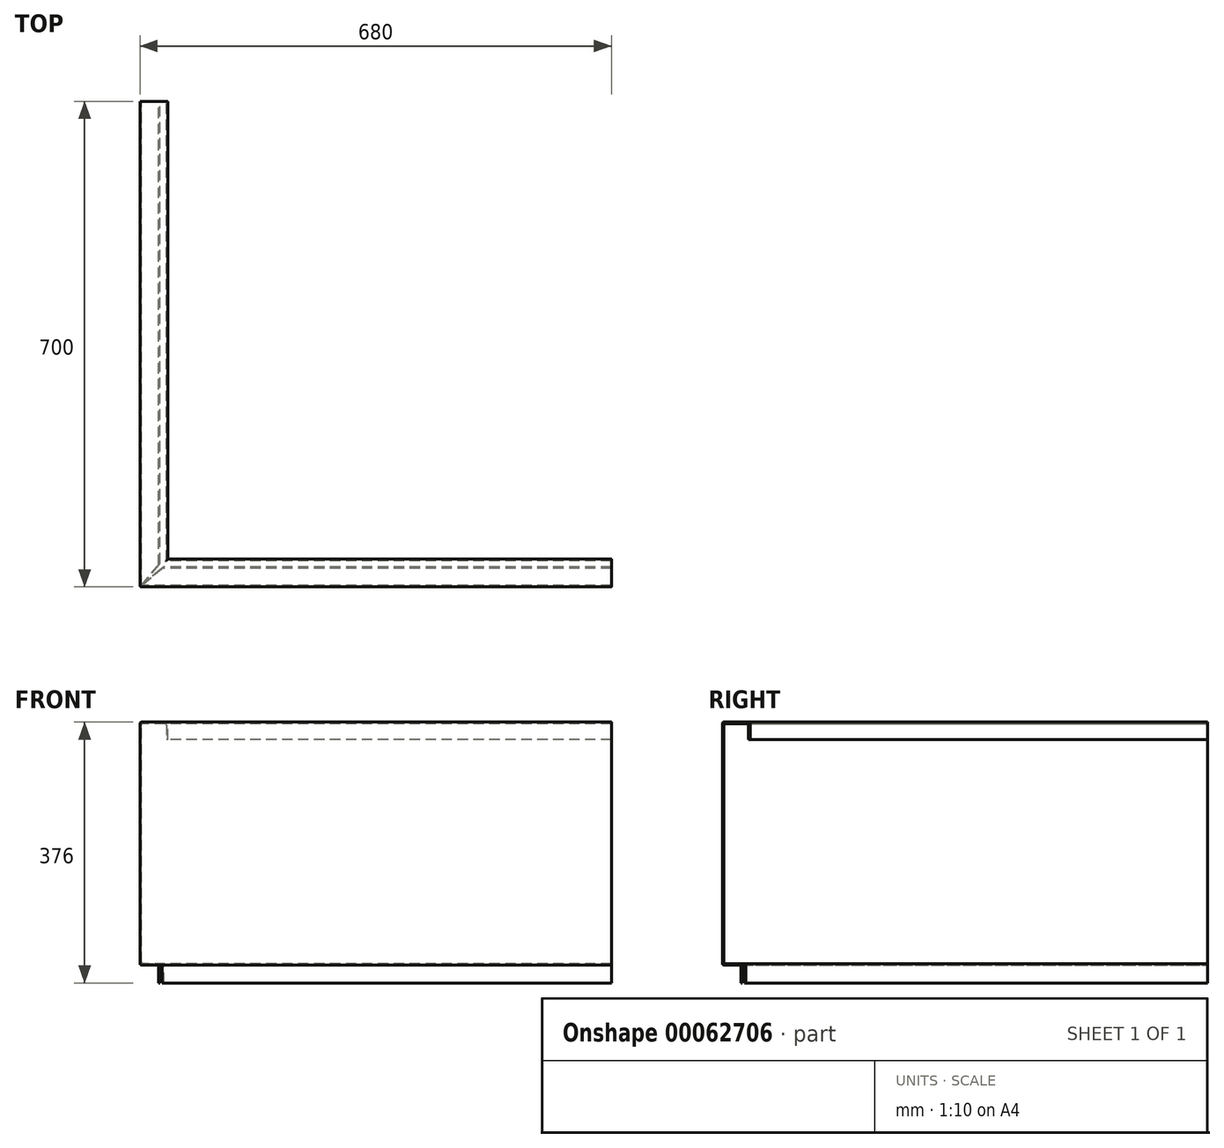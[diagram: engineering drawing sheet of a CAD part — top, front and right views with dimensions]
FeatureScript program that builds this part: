
annotation { "Feature Type Name" : "Feature", "Feature Type Description" : "" }
export const myFeature = defineFeature(function(context is Context, id is Id, definition is map)
    precondition{}
    {
        {
            var Q0;
            Q0=qCreatedBy(makeId("Right.planeOp"),FACE);
            var sketch = newSketch(context, id + "F0", { "sketchPlane" : qUnion([Q0])});
            skLineSegment(sketch, "E0.0", {"start": v(0, -350) * mm, "end": v(27, -350) * mm});
            skLineSegment(sketch, "E0.1", {"start": v(0, 0) * mm, "end": v(0, -350) * mm});
            skLineSegment(sketch, "E1", {"start": v(2, -348) * mm, "end": v(29, -348) * mm});
            skLineSegment(sketch, "E2", {"start": v(2, -2) * mm, "end": v(2, -348) * mm});
            skLineSegment(sketch, "E3", {"start": v(38, -2) * mm, "end": v(2, -2) * mm});
            skLineSegment(sketch, "E4", {"start": v(38, -25) * mm, "end": v(38, -2) * mm});
            skLineSegment(sketch, "E5", {"start": v(27, -350) * mm, "end": v(27, -376) * mm});
            skLineSegment(sketch, "E6", {"start": v(29, -348) * mm, "end": v(29, -376) * mm});
            skLineSegment(sketch, "E0.2", {"start": v(40, 0) * mm, "end": v(0, 0) * mm});
            skLineSegment(sketch, "E0.3", {"start": v(40, -25) * mm, "end": v(40, 0) * mm});
            skLineSegment(sketch, "E7", {"start": v(40, -25) * mm, "end": v(38, -25) * mm});
            skLineSegment(sketch, "E8", {"start": v(29, -376) * mm, "end": v(27, -376) * mm});
            skSolve(sketch);
        }
        {
            var Q0;
            Q0=qCreatedBy(makeId("Top.planeOp"),FACE);
            var sketch = newSketch(context, id + "F1", { "sketchPlane" : qUnion([Q0])});
            skLineSegment(sketch, "E9", {"start": v(0, 0) * mm, "end": v(-680, 0) * mm});
            skLineSegment(sketch, "E10", {"start": v(-680, 0) * mm, "end": v(-680, 700) * mm});
            skSolve(sketch);
        }
        {
            var Q0;
            Q0=qSketchRegion(id+"F0",true);
            var Q1;
            Q1=qConstructionFilter(qBodyType(qCreatedBy(id+"F1",EDGE),BodyType.WIRE),ConstructionObject.NO);
            sweep(context, id + "F2", {"profiles" : qUnion([Q0]), "path" : qUnion([Q1])});
        }
        {
            var Q0;
            Q0=makeQuery(id+"F2.opSweep","SWEPT_FACE",FACE,{"disambiguationData":[OSD([sQuery(id+"F0.wireOp",EDGE,"E1"),sQuery(id+"F1.wireOp",EDGE,"E9")])]});
            var sketch = newSketch(context, id + "F3", { "sketchPlane" : qUnion([Q0])});
            skLineSegment(sketch, "E11", {"start": v(-678, 2) * mm, "end": v(-645.82, 29) * mm});
            skLineSegment(sketch, "E12", {"start": v(-645.82, 29) * mm, "end": v(-651, 29) * mm});
            skLineSegment(sketch, "E13", {"start": v(-651, 29) * mm, "end": v(-651, 34.18) * mm});
            skLineSegment(sketch, "E14", {"start": v(-651, 34.18) * mm, "end": v(-678, 2) * mm});
            skSolve(sketch);
        }
        {
            var Q0;
            Q0=qSketchRegion(id+"F3",true);
            extrude(context, id + "F4", {"entities" : qUnion([Q0]), "operationType" : NewBodyOperationType.REMOVE, "oppositeDirection" : true, "depth" : 30 * mm});
        }
        {
            var Q0;
            Q0=makeQuery(id+"F2.opSweep","SWEPT_EDGE",EDGE,{"disambiguationData":[OSD([sQuery(id+"F0.wireOp",EDGE,"E0.2"),sQuery(id+"F0.wireOp",EDGE,"E0.3"),sQuery(id+"F1.wireOp",EDGE,"E10")])]});
            var Q1;
            Q1=makeQuery(id+"F2.opSweep","SWEPT_EDGE",EDGE,{"disambiguationData":[OSD([sQuery(id+"F0.wireOp",EDGE,"E0.2"),sQuery(id+"F0.wireOp",EDGE,"E0.3"),sQuery(id+"F1.wireOp",EDGE,"E9")])]});
            var Q2;
            Q2=makeQuery(id+"F2.opSweep","SWEPT_EDGE",EDGE,{"disambiguationData":[OSD([sQuery(id+"F0.wireOp",EDGE,"E0.1"),sQuery(id+"F0.wireOp",EDGE,"E0.2"),sQuery(id+"F1.wireOp",EDGE,"E10")])]});
            var Q3;
            Q3=makeQuery(id+"F2.opSweep","SWEPT_EDGE",EDGE,{"disambiguationData":[OSD([sQuery(id+"F0.wireOp",EDGE,"E0.1"),sQuery(id+"F0.wireOp",EDGE,"E0.2"),sQuery(id+"F1.wireOp",EDGE,"E9")])]});
            var Q4;
            Q4=makeQuery(id+"F2.opSweep","SWEPT_EDGE",EDGE,{"disambiguationData":[OSD([sQuery(id+"F0.wireOp",EDGE,"E0.0"),sQuery(id+"F0.wireOp",EDGE,"E0.1"),sQuery(id+"F1.wireOp",EDGE,"E9")])]});
            var Q5;
            Q5=makeQuery(id+"F2.opSweep","SWEPT_EDGE",EDGE,{"disambiguationData":[OSD([sQuery(id+"F0.wireOp",EDGE,"E0.0"),sQuery(id+"F0.wireOp",EDGE,"E5"),sQuery(id+"F1.wireOp",EDGE,"E9")])]});
            var Q6;
            Q6=makeQuery(id+"F2.opSweep","SWEPT_EDGE",EDGE,{"disambiguationData":[OSD([sQuery(id+"F0.wireOp",EDGE,"E0.0"),sQuery(id+"F0.wireOp",EDGE,"E0.1"),sQuery(id+"F1.wireOp",EDGE,"E10")])]});
            var Q7;
            Q7=makeQuery(id+"F2.opSweep","SWEPT_EDGE",EDGE,{"disambiguationData":[OSD([sQuery(id+"F0.wireOp",EDGE,"E0.0"),sQuery(id+"F0.wireOp",EDGE,"E5"),sQuery(id+"F1.wireOp",EDGE,"E10")])]});
            var Q8;
            Q8=makeQuery(id+"F2.opSweep","MID_CAP_EDGE",EDGE,{"disambiguationData":[OSD([sQuery(id+"F0.wireOp",EDGE,"E0.1"),sQuery(id+"F1.wireOp",VERTEX,"E10.start")])],"capPos":1.0});
            var Q9;
            Q9=makeQuery(id+"F2.opSweep","SWEPT_EDGE",EDGE,{"disambiguationData":[OSD([sQuery(id+"F0.wireOp",EDGE,"E1"),sQuery(id+"F0.wireOp",EDGE,"E6"),sQuery(id+"F1.wireOp",EDGE,"E10")])]});
            var Q10;
            Q10=makeQuery(id+"F2.opSweep","SWEPT_EDGE",EDGE,{"disambiguationData":[OSD([sQuery(id+"F0.wireOp",EDGE,"E1"),sQuery(id+"F0.wireOp",EDGE,"E2"),sQuery(id+"F1.wireOp",EDGE,"E10")])]});
            var Q11;
            Q11=makeQuery(id+"F2.opSweep","SWEPT_EDGE",EDGE,{"disambiguationData":[OSD([sQuery(id+"F0.wireOp",EDGE,"E1"),sQuery(id+"F0.wireOp",EDGE,"E6"),sQuery(id+"F1.wireOp",EDGE,"E9")])]});
            var Q12;
            Q12=makeQuery(id+"F2.opSweep","SWEPT_EDGE",EDGE,{"disambiguationData":[OSD([sQuery(id+"F0.wireOp",EDGE,"E1"),sQuery(id+"F0.wireOp",EDGE,"E2"),sQuery(id+"F1.wireOp",EDGE,"E9")])]});
            var Q13;
            Q13=makeQuery(id+"F2.opSweep","SWEPT_EDGE",EDGE,{"disambiguationData":[OSD([sQuery(id+"F0.wireOp",EDGE,"E2"),sQuery(id+"F0.wireOp",EDGE,"E3"),sQuery(id+"F1.wireOp",EDGE,"E9")])]});
            var Q14;
            Q14=makeQuery(id+"F2.opSweep","SWEPT_EDGE",EDGE,{"disambiguationData":[OSD([sQuery(id+"F0.wireOp",EDGE,"E2"),sQuery(id+"F0.wireOp",EDGE,"E3"),sQuery(id+"F1.wireOp",EDGE,"E10")])]});
            var Q15;
            Q15=makeQuery(id+"F2.opSweep","SWEPT_EDGE",EDGE,{"disambiguationData":[OSD([sQuery(id+"F0.wireOp",EDGE,"E3"),sQuery(id+"F0.wireOp",EDGE,"E4"),sQuery(id+"F1.wireOp",EDGE,"E10")])]});
            var Q16;
            Q16=makeQuery(id+"F2.opSweep","SWEPT_EDGE",EDGE,{"disambiguationData":[OSD([sQuery(id+"F0.wireOp",EDGE,"E3"),sQuery(id+"F0.wireOp",EDGE,"E4"),sQuery(id+"F1.wireOp",EDGE,"E9")])]});
            fillet(context, id + "F5", {"entities" : qUnion([Q0, Q1, Q2, Q3, Q4, Q5, Q6, Q7, Q8, Q9, Q10, Q11, Q12, Q13, Q14, Q15, Q16]), "radius" : 2 * mm, "tangentPropagation" : true, "allowEdgeOverflow" : false});
        }
    });
